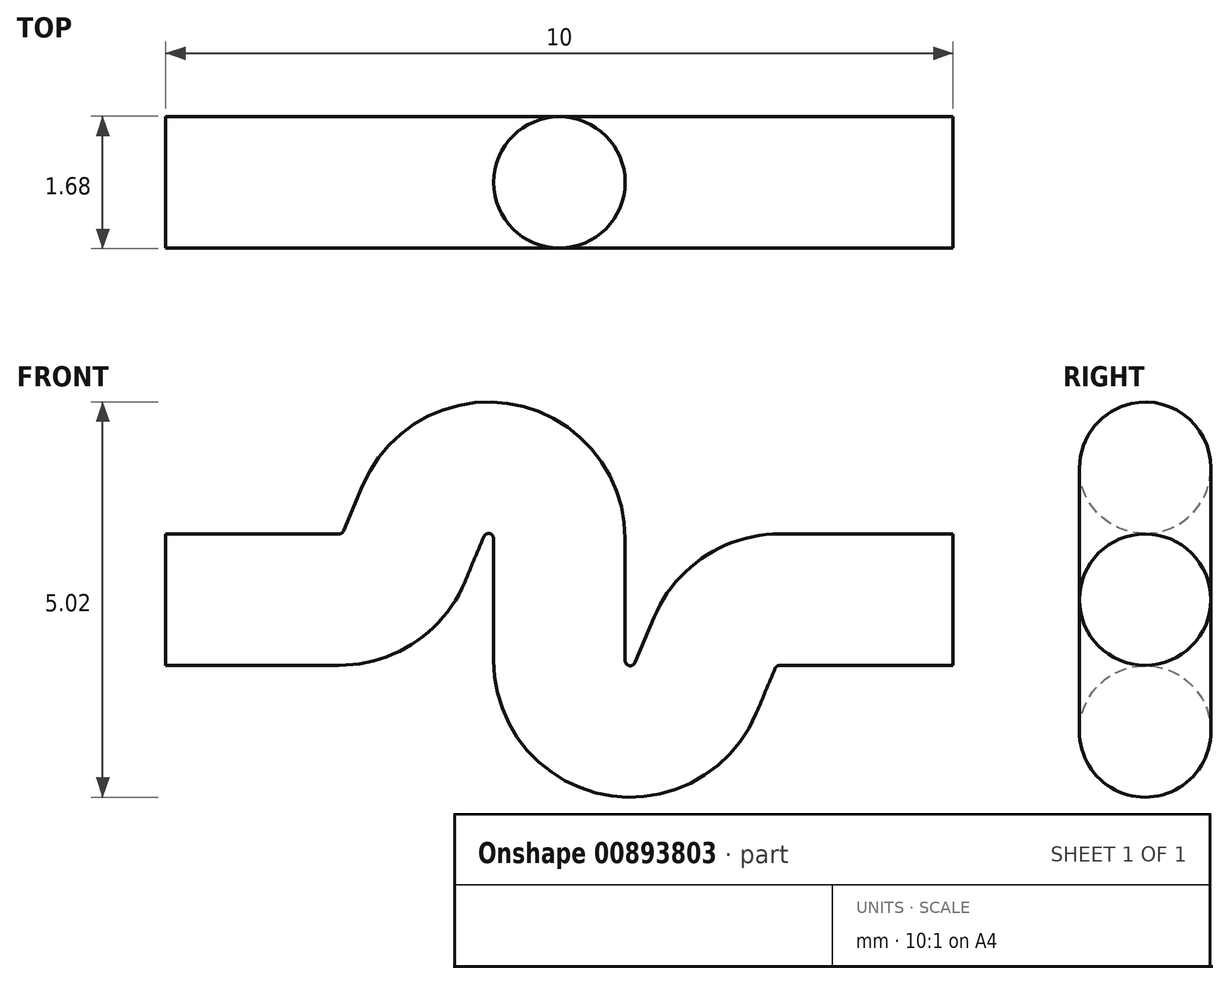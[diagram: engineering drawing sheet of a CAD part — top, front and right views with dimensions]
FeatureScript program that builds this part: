
annotation { "Feature Type Name" : "Feature", "Feature Type Description" : "" }
export const myFeature = defineFeature(function(context is Context, id is Id, definition is map)
    precondition{}
    {
        {
            var Q0;
            Q0=qCreatedBy(makeId("Front.planeOp"),FACE);
            var sketch = newSketch(context, id + "F0", { "sketchPlane" : qUnion([Q0])});
            skLineSegment(sketch, "E0", {"start": v(-2.73, 0.88) * mm, "end": v(5.38, 0.88) * mm, "construction": true});
            skLineSegment(sketch, "E1", {"start": v(0, -0.88) * mm, "end": v(5.12, -0.88) * mm, "construction": true});
            skArc(sketch, "E2.converted", {"start": v(0, 0.77) * mm, "mid": v(-0.72, 1.66) * mm, "end": v(-1.73, 1.12) * mm});
            skLineSegment(sketch, "E3", {"start": v(0, 0.77) * mm, "end": v(0, 0) * mm});
            skLineSegment(sketch, "E4", {"start": v(-2.8, 0) * mm, "end": v(-5, 0) * mm});
            skArc(sketch, "E5", {"start": v(-2.8, 0) * mm, "mid": v(-2.3, 0.15) * mm, "end": v(-1.97, 0.55) * mm});
            skLineSegment(sketch, "E6", {"start": v(-1.73, 1.12) * mm, "end": v(-1.97, 0.55) * mm});
            skArc(sketch, "E7.MirrorCS", {"start": v(0, -0.77) * mm, "mid": v(0.72, -1.66) * mm, "end": v(1.73, -1.12) * mm});
            skArc(sketch, "E8.MirrorCS", {"start": v(2.8, 0) * mm, "mid": v(2.3, -0.15) * mm, "end": v(1.97, -0.55) * mm});
            skLineSegment(sketch, "E9.MirrorCS", {"start": v(1.73, -1.12) * mm, "end": v(1.97, -0.55) * mm});
            skLineSegment(sketch, "E10.MirrorCS", {"start": v(0, -0.77) * mm, "end": v(0, 0) * mm});
            skLineSegment(sketch, "E11", {"start": v(2.8, 0) * mm, "end": v(5, 0) * mm});
            skSolve(sketch);
        }
        {
            var Q0;
            Q0=qCreatedBy(makeId("Right.planeOp"),FACE);
            var Q1;
            Q1=sQuery(id+"F0.wireOp",VERTEX,"E4.end");
            cPlane(context, id + "F1", {"entities" : qUnion([Q0, Q1]), "cplaneType" : CPlaneType.PLANE_POINT, "offset" : 25 * mm, "width" : 150 * mm, "height" : 150 * mm});
        }
        {
            var Q0;
            Q0=qCreatedBy(id+"F1.planeOp",FACE);
            var sketch = newSketch(context, id + "F2", { "sketchPlane" : qUnion([Q0])});
            skCircle(sketch, "E12", {"center": v(0, 0) * mm, "radius": 0.84 * mm});
            skSolve(sketch);
        }
        {
            var Q0;
            Q0=makeQuery(id+"F2.imprint","IMPRINT",FACE,{"disambiguationData":[TD([[makeQuery(id+"F2.imprint","IMPRINT",EDGE,{"derivedFrom":sQuery(id+"F2.wireOp",EDGE,"E12")}),1.0]])]});
            var Q1;
            Q1=sQuery(id+"F0.wireOp",EDGE,"E4");
            var Q2;
            Q2=sQuery(id+"F0.wireOp",EDGE,"E5");
            var Q3;
            Q3=sQuery(id+"F0.wireOp",EDGE,"E6");
            var Q4;
            Q4=sQuery(id+"F0.wireOp",EDGE,"E2.converted");
            var Q5;
            Q5=sQuery(id+"F0.wireOp",EDGE,"E3");
            var Q6;
            Q6=sQuery(id+"F0.wireOp",EDGE,"E10.MirrorCS");
            var Q7;
            Q7=sQuery(id+"F0.wireOp",EDGE,"E7.MirrorCS");
            var Q8;
            Q8=sQuery(id+"F0.wireOp",EDGE,"E9.MirrorCS");
            var Q9;
            Q9=sQuery(id+"F0.wireOp",EDGE,"E8.MirrorCS");
            var Q10;
            Q10=sQuery(id+"F0.wireOp",EDGE,"E11");
            sweep(context, id + "F3", {"profiles" : qUnion([Q0]), "path" : qUnion([Q1, Q2, Q3, Q4, Q5, Q6, Q7, Q8, Q9, Q10])});
        }
    });
